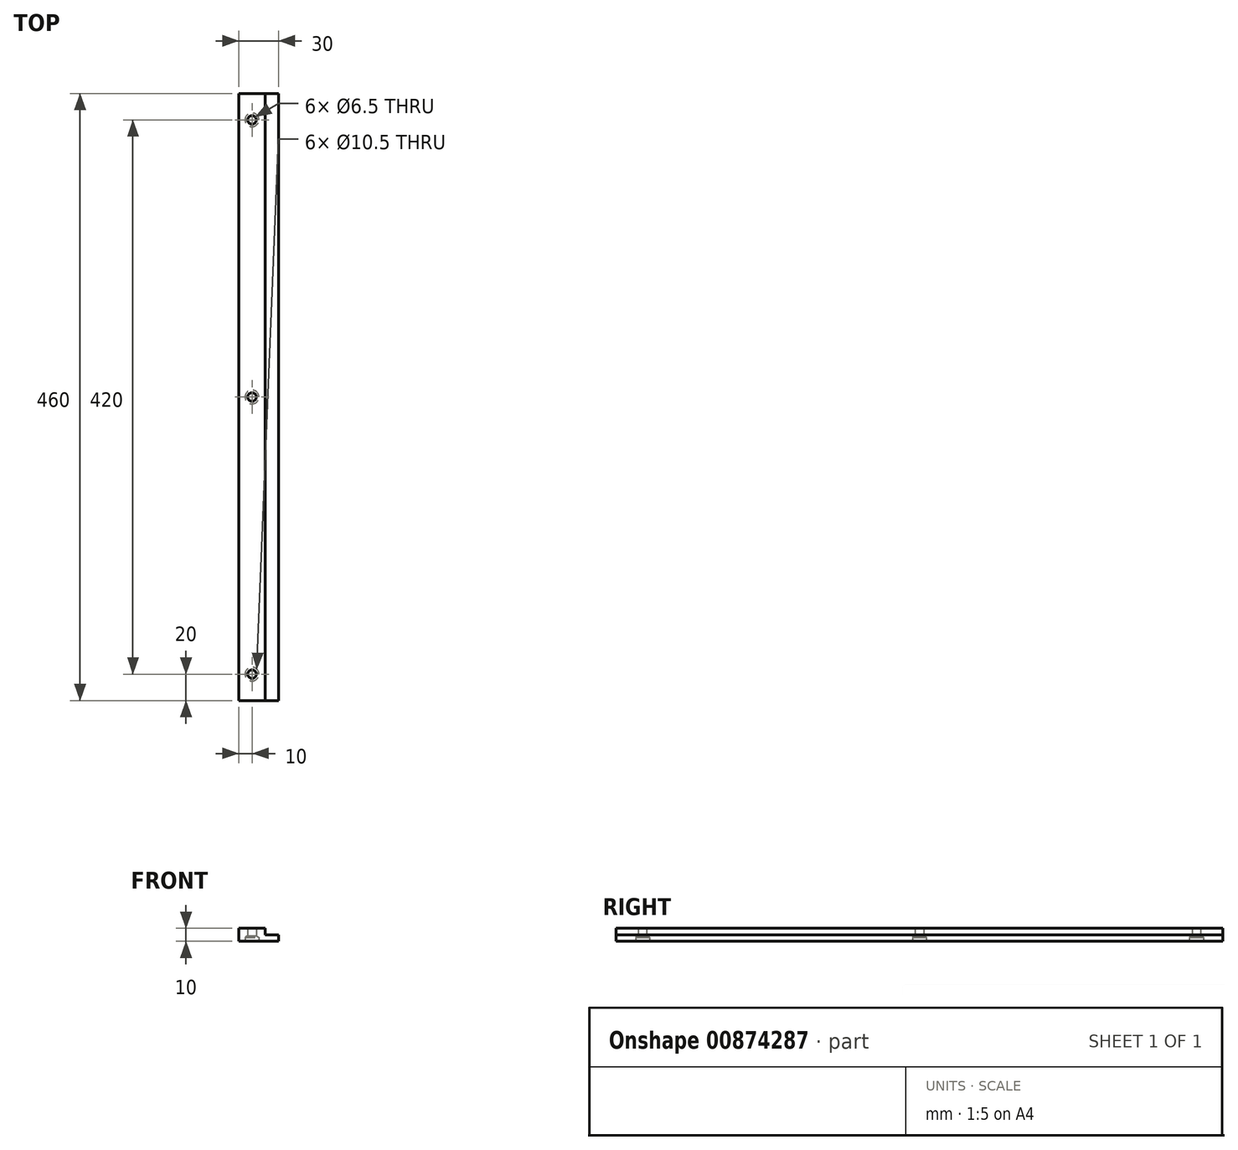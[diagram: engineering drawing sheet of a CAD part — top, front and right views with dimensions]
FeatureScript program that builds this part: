
annotation { "Feature Type Name" : "Feature", "Feature Type Description" : "" }
export const myFeature = defineFeature(function(context is Context, id is Id, definition is map)
    precondition{}
    {
        {
            var Q0;
            Q0=qCreatedBy(makeId("Front.planeOp"),FACE);
            var sketch = newSketch(context, id + "F0", { "sketchPlane" : qUnion([Q0])});
            skLineSegment(sketch, "E0.bottom", {"start": v(0, 0) * mm, "end": v(30, 0) * mm});
            skLineSegment(sketch, "E0.top", {"start": v(0, 10) * mm, "end": v(20, 10) * mm});
            skLineSegment(sketch, "E0.left", {"start": v(0, 0) * mm, "end": v(0, 10) * mm});
            skLineSegment(sketch, "E0.right", {"start": v(30, 0) * mm, "end": v(30, 5) * mm});
            skPoint(sketch, "E1.oppositeSnap0", {"position": v(30, 5) * mm});
            skLineSegment(sketch, "E1.top", {"start": v(30, 5) * mm, "end": v(20, 5) * mm});
            skLineSegment(sketch, "E1.right", {"start": v(20, 10) * mm, "end": v(20, 5) * mm});
            skPoint(sketch, "E2.orphan", {"position": v(30, 10) * mm});
            skSolve(sketch);
        }
        {
            var Q0;
            Q0=makeQuery(id+"F0.imprint","IMPRINT",FACE,{"disambiguationData":[TD([[makeQuery(id+"F0.imprint","IMPRINT",EDGE,{"derivedFrom":sQuery(id+"F0.wireOp",EDGE,"E0.bottom")}),1.0]])]});
            extrude(context, id + "F1", {"entities" : qUnion([Q0]), "oppositeDirection" : true, "depth" : 460 * mm, "offsetDistance" : 25 * mm});
        }
        {
            var Q0;
            Q0=makeQuery(id+"F1.opExtrude","SWEPT_FACE",FACE,{"disambiguationData":[OSD([sQuery(id+"F0.wireOp",EDGE,"E0.bottom")])]});
            var sketch = newSketch(context, id + "F2", { "sketchPlane" : qUnion([Q0])});
            skCircle(sketch, "E3", {"center": v(10, -440) * mm, "radius": 4.25 * mm});
            skSolve(sketch);
        }
        {
            var Q0;
            Q0=sQuery(id+"F2.wireOp",VERTEX,"E3.center");
            var Q1;
            Q1=makeQuery(id+"F1.opExtrude","SWEPT_BODY",BODY,{"disambiguationData":[OSD([sQuery(id+"F0.wireOp",EDGE,"E0.bottom"),sQuery(id+"F0.wireOp",EDGE,"E0.top"),sQuery(id+"F0.wireOp",EDGE,"E0.left"),sQuery(id+"F0.wireOp",EDGE,"E0.right"),sQuery(id+"F0.wireOp",EDGE,"E1.top"),sQuery(id+"F0.wireOp",EDGE,"E1.right")])]});
            hole(context, id + "F3", {"style" : HoleStyle.SIMPLE, "endStyle" : HoleEndStyle.THROUGH, "holeDiameter" : 6.5 * mm, "majorDiameter" : 5 * mm, "isTappedThrough" : true, "tappedDepth" : 12 * mm, "tapClearance" : 3, "locations" : qUnion([Q0]), "scope" : qUnion([Q1])});
        }
        {
            var Q0;
            Q0=makeQuery(id+"F1.opExtrude","SWEPT_FACE",FACE,{"disambiguationData":[OSD([sQuery(id+"F0.wireOp",EDGE,"E0.bottom")])]});
            var sketch = newSketch(context, id + "F4", { "sketchPlane" : qUnion([Q0])});
            skCircle(sketch, "E4", {"center": v(10, -230) * mm, "radius": 4.25 * mm});
            skSolve(sketch);
        }
        {
            var Q0;
            Q0=sQuery(id+"F4.wireOp",VERTEX,"E4.center");
            var Q1;
            Q1=makeQuery(id+"F1.opExtrude","SWEPT_BODY",BODY,{"disambiguationData":[OSD([sQuery(id+"F0.wireOp",EDGE,"E0.bottom"),sQuery(id+"F0.wireOp",EDGE,"E0.top"),sQuery(id+"F0.wireOp",EDGE,"E0.left"),sQuery(id+"F0.wireOp",EDGE,"E0.right"),sQuery(id+"F0.wireOp",EDGE,"E1.top"),sQuery(id+"F0.wireOp",EDGE,"E1.right")])]});
            hole(context, id + "F5", {"style" : HoleStyle.SIMPLE, "endStyle" : HoleEndStyle.THROUGH, "holeDiameter" : 6.5 * mm, "majorDiameter" : 5 * mm, "isTappedThrough" : true, "tappedDepth" : 12 * mm, "tapClearance" : 3, "locations" : qUnion([Q0]), "scope" : qUnion([Q1])});
        }
        {
            var Q0;
            Q0=makeQuery(id+"F1.opExtrude","SWEPT_FACE",FACE,{"disambiguationData":[OSD([sQuery(id+"F0.wireOp",EDGE,"E0.bottom")])]});
            var sketch = newSketch(context, id + "F6", { "sketchPlane" : qUnion([Q0])});
            skCircle(sketch, "E5", {"center": v(10, -20) * mm, "radius": 4.25 * mm});
            skSolve(sketch);
        }
        {
            var Q0;
            Q0=sQuery(id+"F6.wireOp",VERTEX,"E5.center");
            var Q1;
            Q1=makeQuery(id+"F1.opExtrude","SWEPT_BODY",BODY,{"disambiguationData":[OSD([sQuery(id+"F0.wireOp",EDGE,"E0.bottom"),sQuery(id+"F0.wireOp",EDGE,"E0.top"),sQuery(id+"F0.wireOp",EDGE,"E0.left"),sQuery(id+"F0.wireOp",EDGE,"E0.right"),sQuery(id+"F0.wireOp",EDGE,"E1.top"),sQuery(id+"F0.wireOp",EDGE,"E1.right")])]});
            hole(context, id + "F7", {"style" : HoleStyle.SIMPLE, "endStyle" : HoleEndStyle.THROUGH, "holeDiameter" : 6.5 * mm, "majorDiameter" : 5 * mm, "isTappedThrough" : true, "tappedDepth" : 12 * mm, "tapClearance" : 3, "locations" : qUnion([Q0]), "scope" : qUnion([Q1])});
        }
        {
            var Q0;
            Q0=makeQuery(id+"F1.opExtrude","SWEPT_FACE",FACE,{"disambiguationData":[OSD([sQuery(id+"F0.wireOp",EDGE,"E0.bottom")])]});
            var sketch = newSketch(context, id + "F8", { "sketchPlane" : qUnion([Q0])});
            skCircle(sketch, "E6", {"center": v(10, -440) * mm, "radius": 6 * mm});
            skSolve(sketch);
        }
        {
            var Q0;
            Q0=sQuery(id+"F8.wireOp",VERTEX,"E6.center");
            var Q1;
            Q1=makeQuery(id+"F1.opExtrude","SWEPT_BODY",BODY,{"disambiguationData":[OSD([sQuery(id+"F0.wireOp",EDGE,"E0.bottom"),sQuery(id+"F0.wireOp",EDGE,"E0.top"),sQuery(id+"F0.wireOp",EDGE,"E0.left"),sQuery(id+"F0.wireOp",EDGE,"E0.right"),sQuery(id+"F0.wireOp",EDGE,"E1.top"),sQuery(id+"F0.wireOp",EDGE,"E1.right")])]});
            hole(context, id + "F9", {"style" : HoleStyle.SIMPLE, "endStyle" : HoleEndStyle.BLIND, "holeDiameter" : 10.5 * mm, "majorDiameter" : 5 * mm, "holeDepth" : 3 * mm, "isTappedThrough" : true, "tappedDepth" : 12 * mm, "tapClearance" : 3, "startFromSketch" : true, "locations" : qUnion([Q0]), "scope" : qUnion([Q1])});
        }
        {
            var Q0;
            Q0=makeQuery(id+"F1.opExtrude","SWEPT_FACE",FACE,{"disambiguationData":[OSD([sQuery(id+"F0.wireOp",EDGE,"E0.bottom")])]});
            var sketch = newSketch(context, id + "F10", { "sketchPlane" : qUnion([Q0])});
            skCircle(sketch, "E7", {"center": v(10, -230) * mm, "radius": 6 * mm});
            skSolve(sketch);
        }
        {
            var Q0;
            Q0=sQuery(id+"F10.wireOp",VERTEX,"E7.center");
            var Q1;
            Q1=makeQuery(id+"F1.opExtrude","SWEPT_BODY",BODY,{"disambiguationData":[OSD([sQuery(id+"F0.wireOp",EDGE,"E0.bottom"),sQuery(id+"F0.wireOp",EDGE,"E0.top"),sQuery(id+"F0.wireOp",EDGE,"E0.left"),sQuery(id+"F0.wireOp",EDGE,"E0.right"),sQuery(id+"F0.wireOp",EDGE,"E1.top"),sQuery(id+"F0.wireOp",EDGE,"E1.right")])]});
            hole(context, id + "F11", {"style" : HoleStyle.SIMPLE, "endStyle" : HoleEndStyle.BLIND, "holeDiameter" : 10.5 * mm, "majorDiameter" : 5 * mm, "holeDepth" : 3 * mm, "isTappedThrough" : true, "tappedDepth" : 12 * mm, "tapClearance" : 3, "startFromSketch" : true, "locations" : qUnion([Q0]), "scope" : qUnion([Q1])});
        }
        {
            var Q0;
            Q0=makeQuery(id+"F1.opExtrude","SWEPT_FACE",FACE,{"disambiguationData":[OSD([sQuery(id+"F0.wireOp",EDGE,"E0.bottom")])]});
            var sketch = newSketch(context, id + "F12", { "sketchPlane" : qUnion([Q0])});
            skCircle(sketch, "E8", {"center": v(10, -20) * mm, "radius": 6 * mm});
            skSolve(sketch);
        }
        {
            var Q0;
            Q0=sQuery(id+"F12.wireOp",VERTEX,"E8.center");
            var Q1;
            Q1=makeQuery(id+"F1.opExtrude","SWEPT_BODY",BODY,{"disambiguationData":[OSD([sQuery(id+"F0.wireOp",EDGE,"E0.bottom"),sQuery(id+"F0.wireOp",EDGE,"E0.top"),sQuery(id+"F0.wireOp",EDGE,"E0.left"),sQuery(id+"F0.wireOp",EDGE,"E0.right"),sQuery(id+"F0.wireOp",EDGE,"E1.top"),sQuery(id+"F0.wireOp",EDGE,"E1.right")])]});
            hole(context, id + "F13", {"style" : HoleStyle.SIMPLE, "endStyle" : HoleEndStyle.BLIND, "holeDiameter" : 10.5 * mm, "majorDiameter" : 5 * mm, "holeDepth" : 3 * mm, "isTappedThrough" : true, "tappedDepth" : 12 * mm, "tapClearance" : 3, "startFromSketch" : true, "locations" : qUnion([Q0]), "scope" : qUnion([Q1])});
        }
    });
